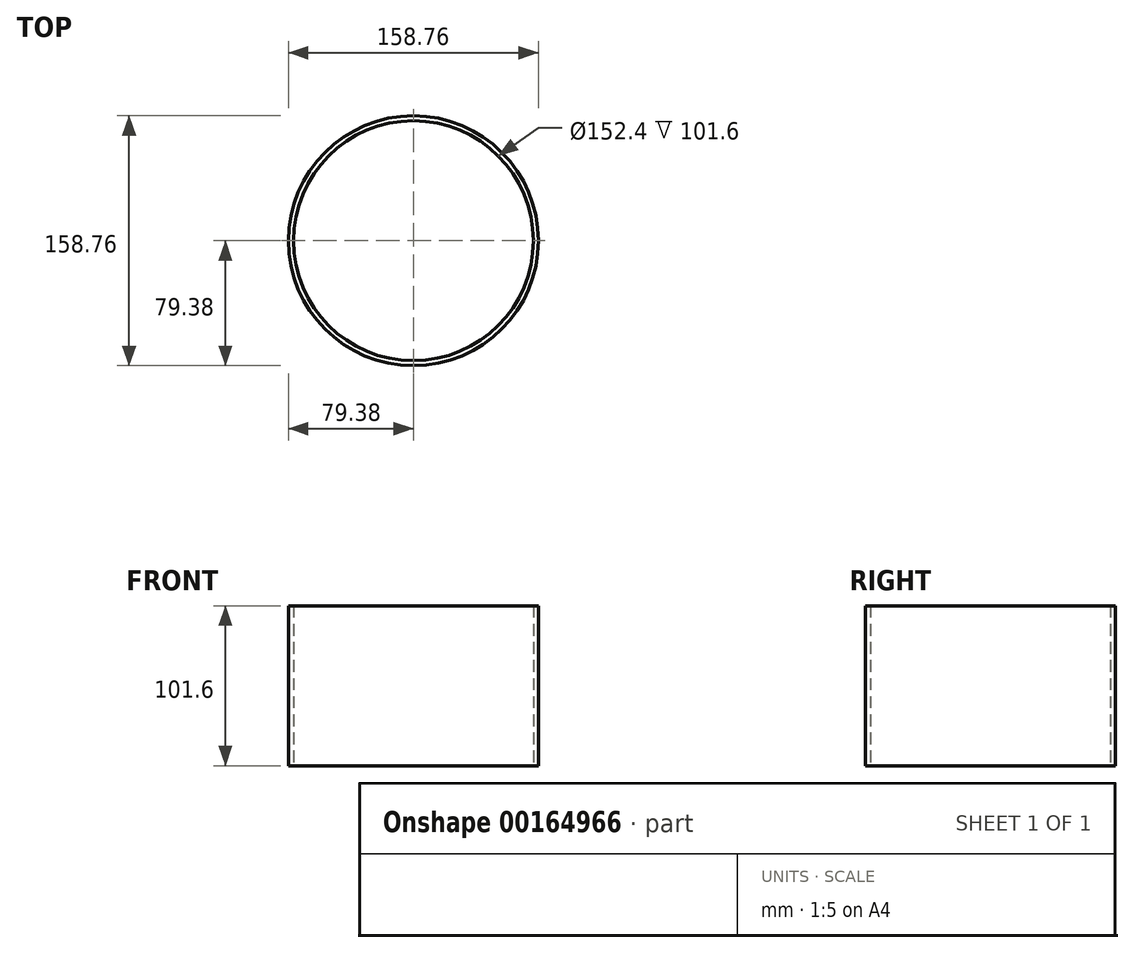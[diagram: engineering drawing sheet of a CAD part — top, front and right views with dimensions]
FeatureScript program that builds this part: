
annotation { "Feature Type Name" : "Feature", "Feature Type Description" : "" }
export const myFeature = defineFeature(function(context is Context, id is Id, definition is map)
    precondition{}
    {
        {
            var Q0;
            Q0=qCreatedBy(makeId("Top.planeOp"),FACE);
            var sketch = newSketch(context, id + "F0", { "sketchPlane" : qUnion([Q0])});
            skCircle(sketch, "E0", {"center": v(0, 0) * mm, "radius": 76.2 * mm});
            skCircle(sketch, "E1", {"center": v(0, 0) * mm, "radius": 79.38 * mm});
            skSolve(sketch);
        }
        {
            var Q0;
            Q0=qSketchRegion(id+"F0",true);
            extrude(context, id + "F1", {"entities" : qUnion([Q0]), "depth" : 101.6 * mm});
        }
    });
